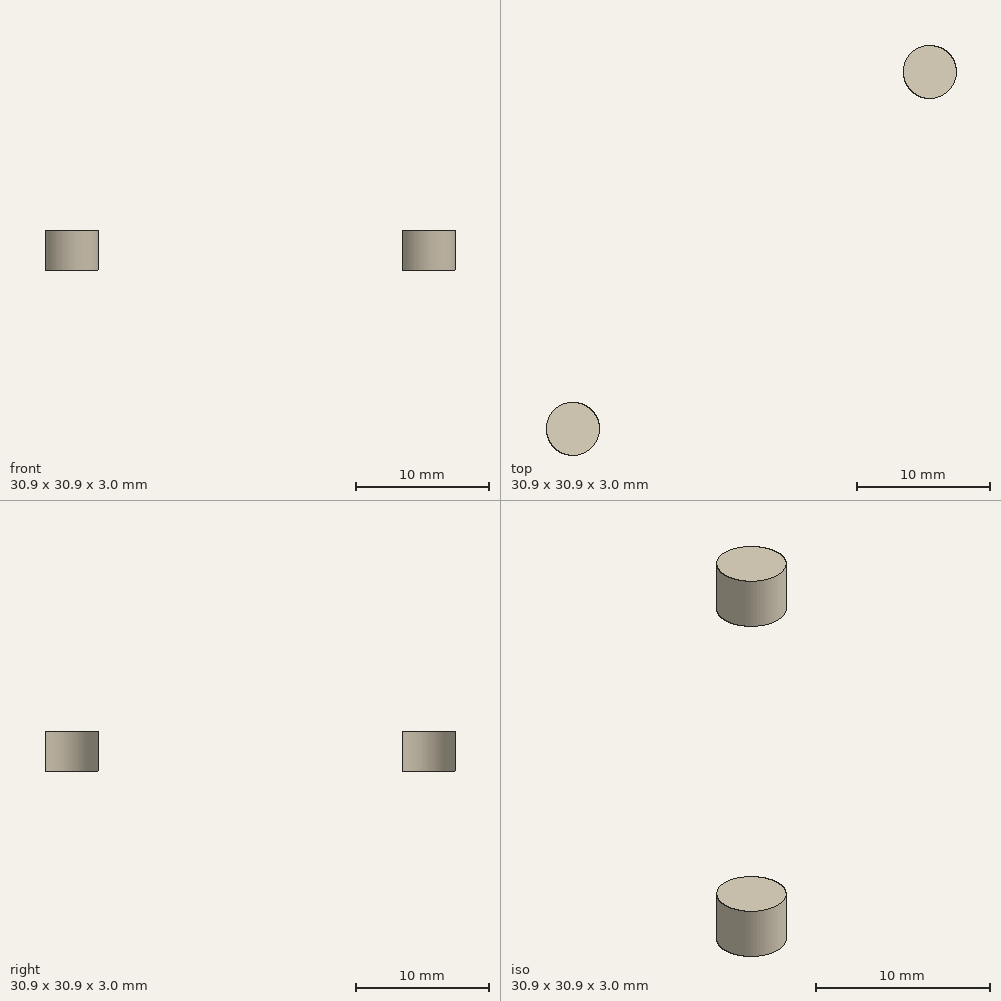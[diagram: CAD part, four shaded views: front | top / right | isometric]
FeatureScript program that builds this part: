
annotation { "Feature Type Name" : "Feature", "Feature Type Description" : "" }
export const myFeature = defineFeature(function(context is Context, id is Id, definition is map)
    precondition{}
    {
        {
            var Q0;
            Q0=qCreatedBy(makeId("Top.planeOp"),FACE);
            var sketch = newSketch(context, id + "F0", { "sketchPlane" : qUnion([Q0])});
            skLineSegment(sketch, "E0.bottom", {"start": v(5, 32.5) * mm, "end": v(-5, 32.5) * mm});
            skLineSegment(sketch, "E0.top", {"start": v(5, -32.5) * mm, "end": v(-5, -32.5) * mm});
            skLineSegment(sketch, "E0.left", {"start": v(20, 17.5) * mm, "end": v(20, 15.45) * mm});
            skLineSegment(sketch, "E0.right", {"start": v(-20, 17.5) * mm, "end": v(-20, -17.5) * mm});
            skPoint(sketch, "E0.middle", {"position": v(0, 0) * mm});
            skArc(sketch, "E1", {"start": v(3, -2.2) * mm, "mid": v(0, 27.5) * mm, "end": v(-3, -2.2) * mm});
            skCircle(sketch, "E2", {"center": v(0, -17.5) * mm, "radius": 10.95 * mm});
            skPoint(sketch, "E3.visualSharp", {"position": v(-20, 32.5) * mm});
            skArc(sketch, "E3.filletArc", {"start": v(-5, 32.5) * mm, "mid": v(-15.6, 28.1) * mm, "end": v(-20, 17.5) * mm});
            skPoint(sketch, "E4.visualSharp", {"position": v(20, 32.5) * mm});
            skArc(sketch, "E4.filletArc", {"start": v(20, 17.5) * mm, "mid": v(15.6, 28.1) * mm, "end": v(5, 32.5) * mm});
            skPoint(sketch, "E5.visualSharp", {"position": v(-20, -32.5) * mm});
            skArc(sketch, "E5.filletArc", {"start": v(-20, -17.5) * mm, "mid": v(-15.6, -28.1) * mm, "end": v(-5, -32.5) * mm});
            skPoint(sketch, "E6.visualSharp", {"position": v(20, -32.5) * mm});
            skArc(sketch, "E6.filletArc", {"start": v(5, -32.5) * mm, "mid": v(15.6, -28.1) * mm, "end": v(20, -17.5) * mm});
            skLineSegment(sketch, "E7", {"start": v(-3, -2.2) * mm, "end": v(-3, -1.4) * mm});
            skLineSegment(sketch, "E8", {"start": v(3, -1.4) * mm, "end": v(3, -2.2) * mm});
            skArc(sketch, "E9.0", {"start": v(-2.88, -1.3) * mm, "mid": v(0, -1.6) * mm, "end": v(2.88, -1.3) * mm});
            skPoint(sketch, "E10.visualSharp", {"position": v(-3, -1.28) * mm});
            skArc(sketch, "E10.filletArc", {"start": v(-2.88, -1.3) * mm, "mid": v(-2.96, -1.32) * mm, "end": v(-3, -1.4) * mm});
            skPoint(sketch, "E11.visualSharp", {"position": v(3, -1.28) * mm});
            skArc(sketch, "E11.filletArc", {"start": v(3, -1.4) * mm, "mid": v(2.96, -1.32) * mm, "end": v(2.88, -1.3) * mm});
            skLineSegment(sketch, "E12", {"start": v(20, -14.5) * mm, "end": v(17, -14.5) * mm});
            skLineSegment(sketch, "E13", {"start": v(17, -14.5) * mm, "end": v(17, 15.45) * mm});
            skLineSegment(sketch, "E14", {"start": v(17, 15.45) * mm, "end": v(20, 15.45) * mm});
            skLineSegment(sketch, "E15.trimOffspring", {"start": v(20, -14.5) * mm, "end": v(20, -17.5) * mm});
            skSolve(sketch);
        }
        {
            var Q0;
            Q0=makeQuery(id+"F0.imprint","IMPRINT",FACE,{"disambiguationData":[TD([[makeQuery(id+"F0.imprint","IMPRINT",EDGE,{"derivedFrom":sQuery(id+"F0.wireOp",EDGE,"E0.bottom")}),1.0]])]});
            extrude(context, id + "F1", {"entities" : qUnion([Q0]), "depth" : 3 * mm, "offsetDistance" : 25 * mm});
        }
        {
            var Q0;
            Q0=makeQuery(id+"F1.opExtrude","CAP_FACE",FACE,{"disambiguationData":[OSD([sQuery(id+"F0.wireOp",EDGE,"E0.bottom"),sQuery(id+"F0.wireOp",EDGE,"E0.top"),sQuery(id+"F0.wireOp",EDGE,"E0.left"),sQuery(id+"F0.wireOp",EDGE,"E0.right"),sQuery(id+"F0.wireOp",EDGE,"E1"),sQuery(id+"F0.wireOp",EDGE,"E2"),sQuery(id+"F0.wireOp",EDGE,"E3.filletArc"),sQuery(id+"F0.wireOp",EDGE,"E4.filletArc"),sQuery(id+"F0.wireOp",EDGE,"E5.filletArc"),sQuery(id+"F0.wireOp",EDGE,"E6.filletArc"),sQuery(id+"F0.wireOp",EDGE,"E7"),sQuery(id+"F0.wireOp",EDGE,"E8"),sQuery(id+"F0.wireOp",EDGE,"E9.0"),sQuery(id+"F0.wireOp",EDGE,"E10.filletArc"),sQuery(id+"F0.wireOp",EDGE,"E11.filletArc")])],"isStart":false});
            var sketch = newSketch(context, id + "F2", { "sketchPlane" : qUnion([Q0])});
            skLineSegment(sketch, "E16", {"start": v(0, 12.5) * mm, "end": v(-15.6, 28.1) * mm, "construction": true});
            skLineSegment(sketch, "E17", {"start": v(0, 12.5) * mm, "end": v(-20, 12.5) * mm, "construction": true});
            skCircle(sketch, "E18", {"center": v(-13.44, 25.94) * mm, "radius": 2 * mm});
            skCircle(sketch, "E19.MirrorC", {"center": v(-13.44, -0.94) * mm, "radius": 2 * mm});
            skCircle(sketch, "E20.MirrorC", {"center": v(13.44, 25.94) * mm, "radius": 2 * mm});
            skCircle(sketch, "E21.MirrorC", {"center": v(13.44, -0.94) * mm, "radius": 2 * mm});
            skSolve(sketch);
        }
        {
            var Q0;
            Q0=makeQuery(id+"F2.imprint","IMPRINT",FACE,{"disambiguationData":[TD([[makeQuery(id+"F2.imprint","IMPRINT",EDGE,{"derivedFrom":sQuery(id+"F2.wireOp",EDGE,"E18")}),1.0]])]});
            var Q1;
            Q1=makeQuery(id+"F2.imprint","IMPRINT",FACE,{"disambiguationData":[TD([[makeQuery(id+"F2.imprint","IMPRINT",EDGE,{"derivedFrom":sQuery(id+"F2.wireOp",EDGE,"E20.MirrorC")}),-1.0]])]});
            var Q2;
            Q2=makeQuery(id+"F2.imprint","IMPRINT",FACE,{"disambiguationData":[TD([[makeQuery(id+"F2.imprint","IMPRINT",EDGE,{"derivedFrom":sQuery(id+"F2.wireOp",EDGE,"E19.MirrorC")}),-1.0]])]});
            var Q3;
            Q3=makeQuery(id+"F2.imprint","IMPRINT",FACE,{"disambiguationData":[TD([[makeQuery(id+"F2.imprint","IMPRINT",EDGE,{"derivedFrom":sQuery(id+"F2.wireOp",EDGE,"E21.MirrorC")}),1.0]])]});
            extrude(context, id + "F3", {"entities" : qUnion([Q0, Q1, Q2, Q3]), "operationType" : NewBodyOperationType.REMOVE, "oppositeDirection" : true, "depth" : 25 * mm, "offsetDistance" : 25 * mm});
        }
    });
